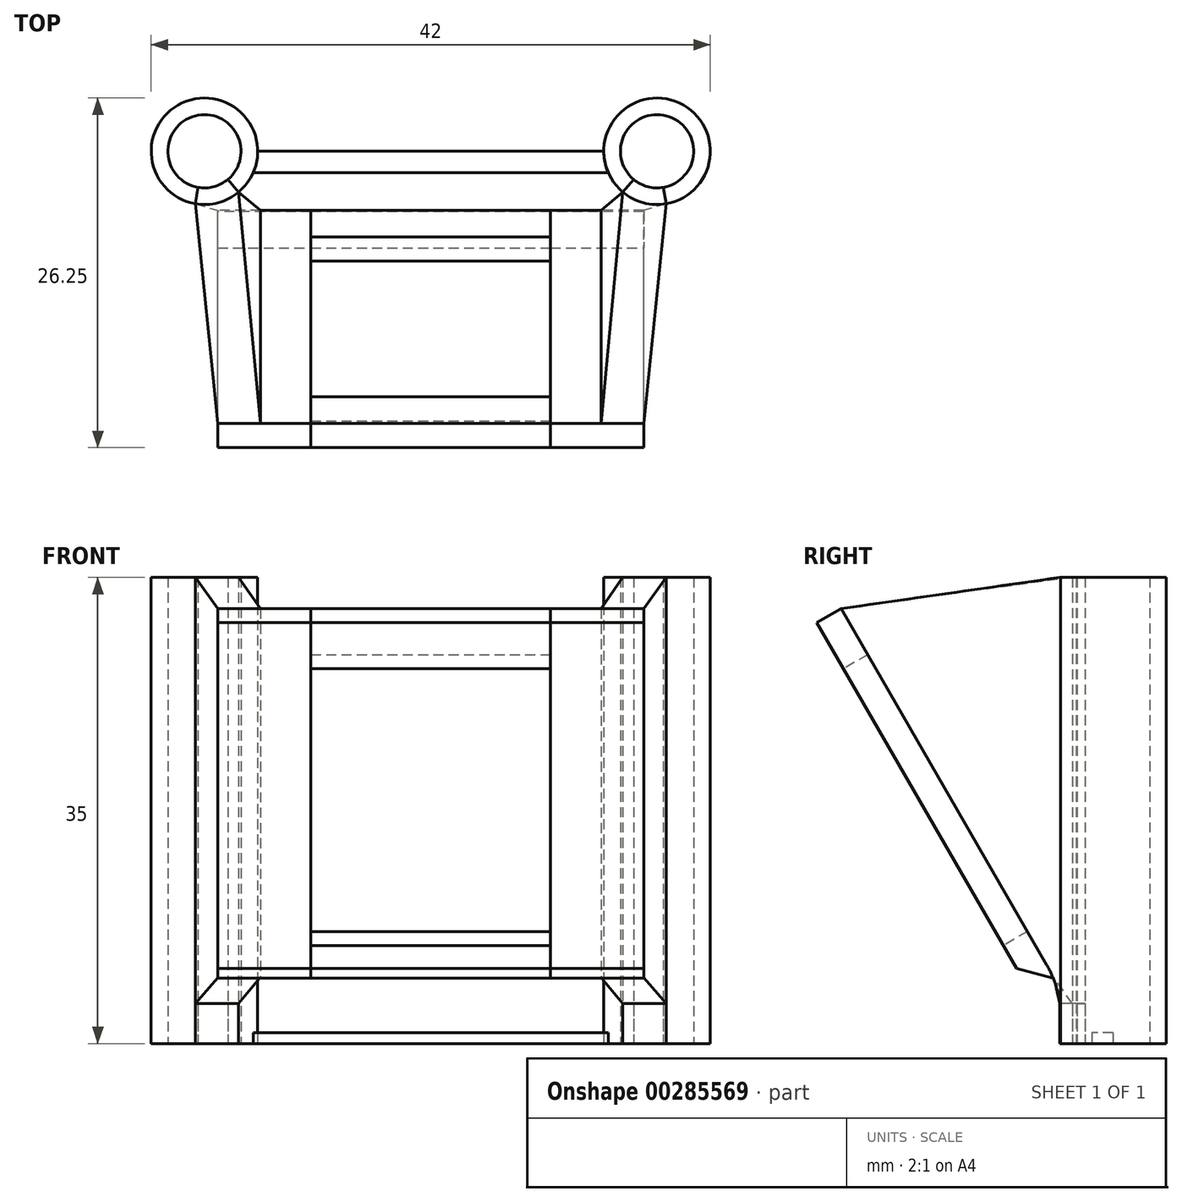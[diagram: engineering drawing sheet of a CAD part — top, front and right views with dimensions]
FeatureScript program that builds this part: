
annotation { "Feature Type Name" : "Feature", "Feature Type Description" : "" }
export const myFeature = defineFeature(function(context is Context, id is Id, definition is map)
    precondition{}
    {
        {
            var Q0;
            Q0=qCreatedBy(makeId("Top.planeOp"),FACE);
            var sketch = newSketch(context, id + "F0", { "sketchPlane" : qUnion([Q0])});
            skCircle(sketch, "E0", {"center": v(0, 0) * mm, "radius": 2.75 * mm});
            skCircle(sketch, "E1.0", {"center": v(0, 0) * mm, "radius": 4 * mm});
            skCircle(sketch, "E2", {"center": v(34, 0) * mm, "radius": 2.75 * mm});
            skCircle(sketch, "E3.0", {"center": v(34, 0) * mm, "radius": 4 * mm});
            skLineSegment(sketch, "E4", {"start": v(0, 0) * mm, "end": v(2.57, -3.06) * mm});
            skLineSegment(sketch, "E5", {"start": v(0, 0) * mm, "end": v(-0.7, -3.94) * mm});
            skLineSegment(sketch, "E6", {"start": v(0, 0) * mm, "end": v(34, 0) * mm, "construction": true});
            skLineSegment(sketch, "E7", {"start": v(34, 0) * mm, "end": v(31.43, -3.06) * mm});
            skLineSegment(sketch, "E8", {"start": v(34, 0) * mm, "end": v(34.7, -3.94) * mm});
            skLineSegment(sketch, "E9", {"start": v(-2.02, -4) * mm, "end": v(35.97, -4) * mm, "construction": true});
            skLineSegment(sketch, "E10", {"start": v(30.33, -1.6) * mm, "end": v(3.67, -1.6) * mm});
            skLineSegment(sketch, "E11", {"start": v(30, 0) * mm, "end": v(4, 0) * mm});
            skSolve(sketch);
        }
        {
            var Q0;
            {var subQ0=sQuery(id+"F0.wireOp",EDGE,"E4");var subQ1=sQuery(id+"F0.wireOp",EDGE,"E0");var subQ2=makeQuery(id+"F0.imprint","INTERSECT",VERTEX,{"derivedFrom":[subQ1,subQ0]});Q0=makeQuery(id+"F0.imprint","IMPRINT",FACE,{"disambiguationData":[TD([[makeQuery(id+"F0.imprint","IMPRINT",EDGE,{"disambiguationData":[TD([[subQ2,-1.0]])],"derivedFrom":subQ1}),-1.0]])]});}
            var Q1;
            {var subQ0=sQuery(id+"F0.wireOp",EDGE,"E7");var subQ1=sQuery(id+"F0.wireOp",EDGE,"E2");var subQ2=makeQuery(id+"F0.imprint","INTERSECT",VERTEX,{"derivedFrom":[subQ1,subQ0]});Q1=makeQuery(id+"F0.imprint","IMPRINT",FACE,{"disambiguationData":[TD([[makeQuery(id+"F0.imprint","IMPRINT",EDGE,{"disambiguationData":[TD([[subQ2,1.0]])],"derivedFrom":subQ1}),-1.0]])]});}
            extrude(context, id + "F1", {"entities" : qUnion([Q0, Q1]), "depth" : 35 * mm});
        }
        {
            var Q0;
            {var subQ0=sQuery(id+"F0.wireOp",EDGE,"E4");var subQ1=sQuery(id+"F0.wireOp",EDGE,"E0");var subQ2=makeQuery(id+"F0.imprint","INTERSECT",VERTEX,{"derivedFrom":[subQ1,subQ0]});Q0=makeQuery(id+"F0.imprint","IMPRINT",FACE,{"disambiguationData":[TD([[makeQuery(id+"F0.imprint","IMPRINT",EDGE,{"disambiguationData":[TD([[subQ2,1.0]])],"derivedFrom":subQ1}),-1.0]])]});}
            var Q1;
            {var subQ0=sQuery(id+"F0.wireOp",EDGE,"E7");var subQ1=sQuery(id+"F0.wireOp",EDGE,"E2");var subQ2=makeQuery(id+"F0.imprint","INTERSECT",VERTEX,{"derivedFrom":[subQ1,subQ0]});Q1=makeQuery(id+"F0.imprint","IMPRINT",FACE,{"disambiguationData":[TD([[makeQuery(id+"F0.imprint","IMPRINT",EDGE,{"disambiguationData":[TD([[subQ2,-1.0]])],"derivedFrom":subQ1}),-1.0]])]});}
            extrude(context, id + "F2", {"entities" : qUnion([Q0, Q1]), "depth" : 3 * mm});
        }
        {
            var Q0;
            Q0=sQuery(id+"F0.wireOp",EDGE,"E9");
            cPlane(context, id + "F3", {"entities" : qUnion([Q0]), "cplaneType" : CPlaneType.LINE_ANGLE, "offset" : 25 * mm, "angle" : 30 * degree, "width" : 150 * mm, "height" : 150 * mm});
        }
        {
            var Q0;
            Q0=qCreatedBy(id+"F3.planeOp",FACE);
            var sketch = newSketch(context, id + "F4", { "sketchPlane" : qUnion([Q0])});
            skLineSegment(sketch, "E12.bottom", {"start": v(-33, 38.5) * mm, "end": v(-4.2, 38.5) * mm});
            skLineSegment(sketch, "E12.top", {"start": v(-33, 6.5) * mm, "end": v(-29.8, 6.5) * mm});
            skLineSegment(sketch, "E12.left", {"start": v(-33, 38.5) * mm, "end": v(-33, 6.5) * mm});
            skLineSegment(sketch, "E12.right", {"start": v(-1, 38.5) * mm, "end": v(-1, 6.5) * mm});
            skLineSegment(sketch, "E13", {"start": v(-29.8, 38.5) * mm, "end": v(-29.8, 38.5) * mm});
            skLineSegment(sketch, "E14", {"start": v(-4.2, 38.5) * mm, "end": v(-4.2, 6.5) * mm});
            skLineSegment(sketch, "E15", {"start": v(-4.2, 6.5) * mm, "end": v(-4.2, 6.5) * mm});
            skLineSegment(sketch, "E16", {"start": v(-4.2, 6.5) * mm, "end": v(-1, 6.5) * mm});
            skLineSegment(sketch, "E17", {"start": v(-29.8, 6.5) * mm, "end": v(-4.2, 6.5) * mm});
            skLineSegment(sketch, "E18", {"start": v(-29.8, 38.5) * mm, "end": v(-29.8, 6.5) * mm});
            skLineSegment(sketch, "E19", {"start": v(-4.2, 38.5) * mm, "end": v(-1, 38.5) * mm});
            skLineSegment(sketch, "E20", {"start": v(-26, 6.5) * mm, "end": v(-26, 38.5) * mm});
            skLineSegment(sketch, "E21", {"start": v(-8, 38.5) * mm, "end": v(-8, 6.5) * mm});
            skSolve(sketch);
        }
        {
            var Q0;
            Q0=makeQuery(id+"F4.imprint","IMPRINT",FACE,{"disambiguationData":[TD([[makeQuery(id+"F4.imprint","IMPRINT",EDGE,{"derivedFrom":sQuery(id+"F4.wireOp",EDGE,"E12.top")}),1.0]])]});
            extrude(context, id + "F5", {"entities" : qUnion([Q0]), "depth" : 2.1 * mm});
        }
        {
            var Q0;
            Q0=makeQuery(id+"F2.opExtrude","CAP_FACE",FACE,{"disambiguationData":[OSD([sQuery(id+"F0.wireOp",EDGE,"E2"),sQuery(id+"F0.wireOp",EDGE,"E3.0"),sQuery(id+"F0.wireOp",EDGE,"E7"),sQuery(id+"F0.wireOp",EDGE,"E8")])],"isStart":false});
            var Q1;
            Q1=makeQuery(id+"F2.opExtrude","CAP_FACE",FACE,{"disambiguationData":[OSD([sQuery(id+"F0.wireOp",EDGE,"E0"),sQuery(id+"F0.wireOp",EDGE,"E1.0"),sQuery(id+"F0.wireOp",EDGE,"E4"),sQuery(id+"F0.wireOp",EDGE,"E5")])],"isStart":false});
            extrude(context, id + "F6", {"entities" : qUnion([Q0, Q1]), "depth" : 32 * mm});
        }
        {
            var Q0;
            Q0=makeQuery(id+"F6.opExtrude","SWEPT_FACE",FACE,{"disambiguationData":[OSD([sQuery(id+"F0.wireOp",EDGE,"E3.0")])]});
            var Q1;
            Q1=makeQuery(id+"F5.opExtrude","CAP_FACE",FACE,{"disambiguationData":[OSD([sQuery(id+"F4.wireOp",EDGE,"E12.bottom"),sQuery(id+"F4.wireOp",EDGE,"E12.top"),sQuery(id+"F4.wireOp",EDGE,"E12.left"),sQuery(id+"F4.wireOp",EDGE,"E18")])],"isStart":false});
            loft(context, id + "F7", {"sheetProfilesArray" : [{ "sheetProfileEntities" : qUnion([Q0]) }, { "sheetProfileEntities" : qUnion([Q1]) }]});
        }
        {
            var Q0;
            {var subQ0=sQuery(id+"F4.wireOp",EDGE,"E18");Q0=makeQuery(id+"F4.imprint","IMPRINT",FACE,{"disambiguationData":[TD([[makeQuery(id+"F4.imprint","IMPRINT",EDGE,{"derivedFrom":subQ0}),1.0]])]});}
            extrude(context, id + "F8", {"entities" : qUnion([Q0]), "operationType" : NewBodyOperationType.ADD, "depth" : 2.1 * mm});
        }
        {
            var Q0;
            Q0=makeQuery(id+"F4.imprint","IMPRINT",FACE,{"disambiguationData":[TD([[makeQuery(id+"F4.imprint","IMPRINT",EDGE,{"derivedFrom":sQuery(id+"F4.wireOp",EDGE,"E12.right")}),-1.0]])]});
            extrude(context, id + "F9", {"entities" : qUnion([Q0]), "depth" : 2.1 * mm});
        }
        {
            var Q0;
            Q0=makeQuery(id+"F6.opExtrude","SWEPT_FACE",FACE,{"disambiguationData":[OSD([sQuery(id+"F0.wireOp",EDGE,"E1.0")])]});
            var Q1;
            Q1=makeQuery(id+"F9.opExtrude","CAP_FACE",FACE,{"disambiguationData":[OSD([sQuery(id+"F4.wireOp",EDGE,"E12.right"),sQuery(id+"F4.wireOp",EDGE,"E14"),sQuery(id+"F4.wireOp",EDGE,"E16"),sQuery(id+"F4.wireOp",EDGE,"E19")])],"isStart":false});
            loft(context, id + "F10", {"sheetProfilesArray" : [{ "sheetProfileEntities" : qUnion([Q0]) }, { "sheetProfileEntities" : qUnion([Q1]) }]});
        }
        {
            var Q0;
            {var subQ0=sQuery(id+"F4.wireOp",EDGE,"E14");Q0=makeQuery(id+"F4.imprint","IMPRINT",FACE,{"disambiguationData":[TD([[makeQuery(id+"F4.imprint","IMPRINT",EDGE,{"derivedFrom":subQ0}),-1.0]])]});}
            extrude(context, id + "F11", {"entities" : qUnion([Q0]), "operationType" : NewBodyOperationType.ADD, "depth" : 2.1 * mm});
        }
        {
            var Q0;
            Q0=makeQuery(id+"F8.opExtrude","SWEPT_FACE",FACE,{"disambiguationData":[OSD([sQuery(id+"F4.wireOp",EDGE,"E20")])]});
            var sketch = newSketch(context, id + "F12", { "sketchPlane" : qUnion([Q0])});
            skLineSegment(sketch, "E22", {"start": v(4.43, 4.95) * mm, "end": v(6.43, 8.41) * mm});
            skLineSegment(sketch, "E23", {"start": v(6.43, 8.41) * mm, "end": v(8.25, 7.36) * mm});
            skLineSegment(sketch, "E24", {"start": v(8.25, 7.36) * mm, "end": v(6.25, 3.9) * mm});
            skLineSegment(sketch, "E25", {"start": v(6.25, 3.9) * mm, "end": v(4.43, 4.95) * mm});
            skLineSegment(sketch, "E26", {"start": v(20.43, 32.66) * mm, "end": v(18.43, 29.2) * mm});
            skLineSegment(sketch, "E27", {"start": v(18.43, 29.2) * mm, "end": v(20.25, 28.15) * mm});
            skLineSegment(sketch, "E28", {"start": v(20.25, 28.15) * mm, "end": v(22.25, 31.6) * mm});
            skLineSegment(sketch, "E29", {"start": v(22.25, 31.6) * mm, "end": v(20.43, 32.66) * mm});
            skSolve(sketch);
        }
        {
            var Q0;
            Q0 = qSketchRegion(id + "F12", true);
            extrude(context, id + "F13", {"entities" : qUnion([Q0]), "depth" : 18 * mm});
        }
        {
            var Q0;
            {var subQ0=sQuery(id+"F0.wireOp",EDGE,"E10");Q0=makeQuery(id+"F0.imprint","IMPRINT",FACE,{"disambiguationData":[TD([[makeQuery(id+"F0.imprint","IMPRINT",EDGE,{"derivedFrom":subQ0}),-1.0]])]});}
            extrude(context, id + "F14", {"entities" : qUnion([Q0]), "depth" : 0.8 * mm});
        }
        {
            var Q0;
            Q0=makeQuery(id+"F11.boolean.opBoolean","MERGE",EDGE,{"derivedFrom":[makeQuery(id+"F9.opExtrude","CAP_EDGE",EDGE,{"disambiguationData":[OSD([sQuery(id+"F4.wireOp",EDGE,"E16")])],"isStart":true}),makeQuery(id+"F11.opExtrude","CAP_EDGE",EDGE,{"disambiguationData":[OSD([sQuery(id+"F4.wireOp",EDGE,"E17")])],"isStart":true})]});
            var Q1;
            Q1=makeQuery(id+"F13.opExtrude","SWEPT_EDGE",EDGE,{"disambiguationData":[OSD([sQuery(id+"F12.wireOp",EDGE,"E24"),sQuery(id+"F12.wireOp",EDGE,"E25")])]});
            var Q2;
            Q2=makeQuery(id+"F8.boolean.opBoolean","MERGE",EDGE,{"derivedFrom":[makeQuery(id+"F5.opExtrude","CAP_EDGE",EDGE,{"disambiguationData":[OSD([sQuery(id+"F4.wireOp",EDGE,"E12.top")])],"isStart":true}),makeQuery(id+"F8.opExtrude","CAP_EDGE",EDGE,{"disambiguationData":[OSD([sQuery(id+"F4.wireOp",EDGE,"E17")])],"isStart":true})]});
            chamfer(context, id + "F15", {"entities" : qUnion([Q0, Q1, Q2]), "width" : 2 * mm, "tangentPropagation" : true});
        }
    });
